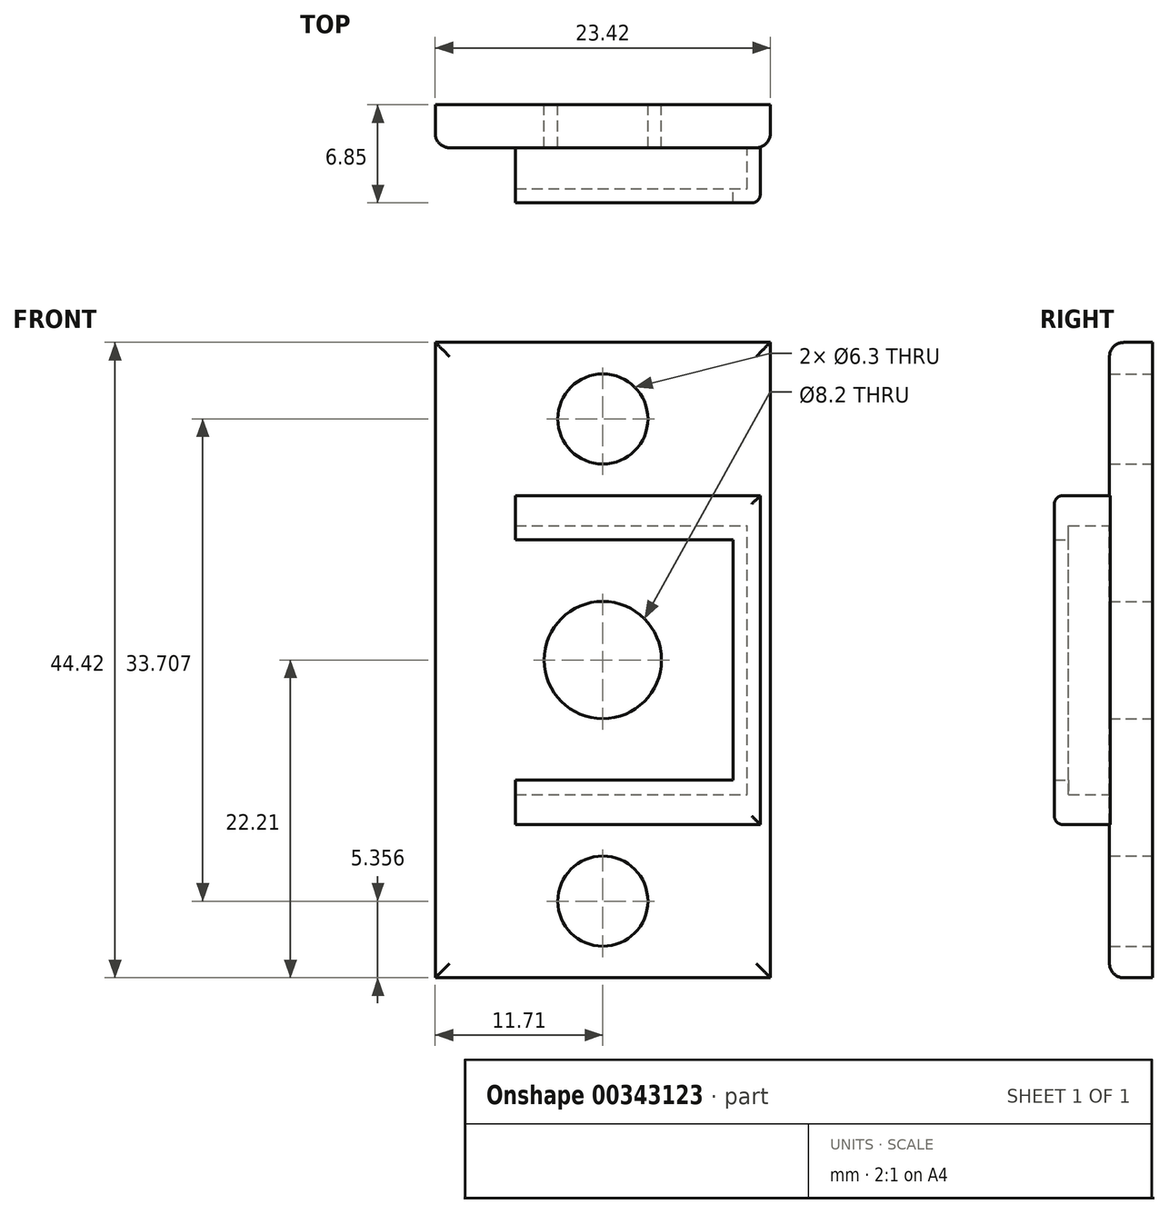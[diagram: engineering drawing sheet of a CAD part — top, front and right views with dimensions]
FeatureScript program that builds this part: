
annotation { "Feature Type Name" : "Feature", "Feature Type Description" : "" }
export const myFeature = defineFeature(function(context is Context, id is Id, definition is map)
    precondition{}
    {
        {
            var Q0;
            Q0=qCreatedBy(makeId("Front.planeOp"),FACE);
            var sketch = newSketch(context, id + "F0", { "sketchPlane" : qUnion([Q0])});
            skLineSegment(sketch, "E0.bottom", {"start": v(0, 0) * mm, "end": v(22, 0) * mm});
            skLineSegment(sketch, "E0.top", {"start": v(0, 23) * mm, "end": v(22, 23) * mm});
            skLineSegment(sketch, "E0.left", {"start": v(0, 0) * mm, "end": v(0, 23) * mm});
            skLineSegment(sketch, "E0.right", {"start": v(22, 0) * mm, "end": v(22, 23) * mm});
            skLineSegment(sketch, "E1.bottom", {"start": v(21.1, 20.9) * mm, "end": v(0.9, 20.9) * mm});
            skLineSegment(sketch, "E1.top", {"start": v(21.1, 2.1) * mm, "end": v(0.9, 2.1) * mm});
            skLineSegment(sketch, "E1.left", {"start": v(21.1, 20.9) * mm, "end": v(21.1, 2.1) * mm});
            skLineSegment(sketch, "E1.right", {"start": v(0.9, 20.9) * mm, "end": v(0.9, 2.1) * mm});
            skPoint(sketch, "E2", {"position": v(4.9, 20.9) * mm});
            skPoint(sketch, "E3", {"position": v(4.9, 2.1) * mm});
            skPoint(sketch, "E4", {"position": v(22, 1.5) * mm});
            skPoint(sketch, "E5", {"position": v(22, 21.5) * mm});
            skPoint(sketch, "E6", {"position": v(0, 1.5) * mm});
            skPoint(sketch, "E7", {"position": v(11, 11.5) * mm});
            skLineSegment(sketch, "E8", {"start": v(4.9, 20.9) * mm, "end": v(4.9, 23) * mm});
            skLineSegment(sketch, "E9", {"start": v(4.9, 2.1) * mm, "end": v(4.9, 0) * mm});
            skPoint(sketch, "E10", {"position": v(11, 20.9) * mm});
            skPoint(sketch, "E11", {"position": v(11, 2.1) * mm});
            skLineSegment(sketch, "E12.bottom", {"start": v(22.7, 33.7) * mm, "end": v(-0.7, 33.7) * mm});
            skLineSegment(sketch, "E12.top", {"start": v(22.7, -10.7) * mm, "end": v(-0.7, -10.7) * mm});
            skLineSegment(sketch, "E12.left", {"start": v(22.7, 33.7) * mm, "end": v(22.7, -10.7) * mm});
            skLineSegment(sketch, "E12.right", {"start": v(-0.7, 33.7) * mm, "end": v(-0.7, -10.7) * mm});
            skPoint(sketch, "E13", {"position": v(11, -5.35) * mm});
            skPoint(sketch, "E14", {"position": v(11, 28.35) * mm});
            skLineSegment(sketch, "E15", {"start": v(11, 29.06) * mm, "end": v(11, 27.39) * mm});
            skLineSegment(sketch, "E16", {"start": v(11, -4.63) * mm, "end": v(11, -5.92) * mm});
            skSolve(sketch);
        }
        {
            var Q0;
            Q0=makeQuery(id+"F0.imprint","IMPRINT",FACE,{"disambiguationData":[TD([[makeQuery(id+"F0.imprint","IMPRINT",EDGE,{"derivedFrom":sQuery(id+"F0.wireOp",EDGE,"E1.bottom")}),1.0]])]});
            var Q1;
            Q1=makeQuery(id+"F0.imprint","IMPRINT",FACE,{"disambiguationData":[TD([[makeQuery(id+"F0.imprint","IMPRINT",EDGE,{"derivedFrom":sQuery(id+"F0.wireOp",EDGE,"E0.bottom")}),1.0]])]});
            extrude(context, id + "F1", {"entities" : qUnion([Q0, Q1]), "depth" : 3 * mm});
        }
        {
            var Q0;
            {var subQ0=sQuery(id+"F0.wireOp",EDGE,"E0.right");Q0=makeQuery(id+"F0.imprint","IMPRINT",FACE,{"disambiguationData":[TD([[makeQuery(id+"F0.imprint","IMPRINT",EDGE,{"derivedFrom":subQ0}),1.0]])]});}
            extrude(context, id + "F2", {"entities" : qUnion([Q0]), "operationType" : NewBodyOperationType.ADD, "depth" : 6.85 * mm});
        }
        {
            var Q0;
            Q0=makeQuery(id+"F2.opExtrude","SWEPT_FACE",FACE,{"disambiguationData":[OSD([sQuery(id+"F0.wireOp",EDGE,"E1.bottom")])]});
            var sketch = newSketch(context, id + "F3", { "sketchPlane" : qUnion([Q0])});
            skLineSegment(sketch, "E17.bottom", {"start": v(21.1, 6.85) * mm, "end": v(21.1, 6.85) * mm});
            skLineSegment(sketch, "E17.top", {"start": v(21.1, 5.85) * mm, "end": v(21.1, 5.85) * mm});
            skLineSegment(sketch, "E17.left", {"start": v(21.1, 6.85) * mm, "end": v(21.1, 5.85) * mm});
            skLineSegment(sketch, "E17.right", {"start": v(21.1, 6.85) * mm, "end": v(21.1, 5.85) * mm});
            skLineSegment(sketch, "E18.bottom", {"start": v(4.9, 6.85) * mm, "end": v(21.1, 6.85) * mm});
            skLineSegment(sketch, "E18.top", {"start": v(4.9, 5.85) * mm, "end": v(21.1, 5.85) * mm});
            skLineSegment(sketch, "E18.left", {"start": v(4.9, 6.85) * mm, "end": v(4.9, 5.85) * mm});
            skSolve(sketch);
        }
        {
            var Q0;
            Q0=makeQuery(id+"F2.opExtrude","SWEPT_FACE",FACE,{"disambiguationData":[OSD([sQuery(id+"F0.wireOp",EDGE,"E1.left")])]});
            var sketch = newSketch(context, id + "F4", { "sketchPlane" : qUnion([Q0])});
            skLineSegment(sketch, "E19.bottom", {"start": v(6.85, 2.1) * mm, "end": v(5.85, 2.1) * mm});
            skLineSegment(sketch, "E19.top", {"start": v(6.85, 20.9) * mm, "end": v(5.85, 20.9) * mm});
            skLineSegment(sketch, "E19.left", {"start": v(6.85, 2.1) * mm, "end": v(6.85, 20.9) * mm});
            skLineSegment(sketch, "E19.right", {"start": v(5.85, 2.1) * mm, "end": v(5.85, 20.9) * mm});
            skSolve(sketch);
        }
        {
            var Q0;
            Q0=makeQuery(id+"F2.opExtrude","SWEPT_FACE",FACE,{"disambiguationData":[OSD([sQuery(id+"F0.wireOp",EDGE,"E1.top")])]});
            var sketch = newSketch(context, id + "F5", { "sketchPlane" : qUnion([Q0])});
            skLineSegment(sketch, "E20.bottom", {"start": v(21.1, -6.85) * mm, "end": v(21.1, -6.85) * mm});
            skLineSegment(sketch, "E20.top", {"start": v(21.1, -5.85) * mm, "end": v(21.1, -5.85) * mm});
            skLineSegment(sketch, "E20.left", {"start": v(21.1, -6.85) * mm, "end": v(21.1, -5.85) * mm});
            skLineSegment(sketch, "E20.right", {"start": v(21.1, -6.85) * mm, "end": v(21.1, -5.85) * mm});
            skLineSegment(sketch, "E21.bottom", {"start": v(4.9, -6.85) * mm, "end": v(21.1, -6.85) * mm});
            skLineSegment(sketch, "E21.top", {"start": v(4.9, -5.85) * mm, "end": v(21.1, -5.85) * mm});
            skLineSegment(sketch, "E21.left", {"start": v(4.9, -6.85) * mm, "end": v(4.9, -5.85) * mm});
            skSolve(sketch);
        }
        {
            var Q0;
            {var subQ4=sQuery(id+"F0.wireOp",EDGE,"E0.left");Q0=makeQuery(id+"F0.imprint","IMPRINT",FACE,{"disambiguationData":[TD([[makeQuery(id+"F0.imprint","IMPRINT",EDGE,{"derivedFrom":subQ4}),-1.0]])]});}
            extrude(context, id + "F6", {"entities" : qUnion([Q0]), "operationType" : NewBodyOperationType.ADD, "depth" : 3 * mm});
        }
        {
            var Q0;
            Q0=makeQuery(id+"F3.imprint","IMPRINT",FACE,{"disambiguationData":[TD([[makeQuery(id+"F3.imprint","IMPRINT",EDGE,{"derivedFrom":sQuery(id+"F3.wireOp",EDGE,"E17.bottom")}),1.0]])]});
            var Q1;
            Q1=makeQuery(id+"F3.imprint","IMPRINT",FACE,{"disambiguationData":[TD([[makeQuery(id+"F3.imprint","IMPRINT",EDGE,{"derivedFrom":sQuery(id+"F3.wireOp",EDGE,"E18.bottom")}),1.0]])]});
            extrude(context, id + "F7", {"entities" : qUnion([Q0, Q1]), "operationType" : NewBodyOperationType.ADD, "depth" : 1 * mm});
        }
        {
            var Q0;
            Q0=makeQuery(id+"F5.imprint","IMPRINT",FACE,{"disambiguationData":[TD([[makeQuery(id+"F5.imprint","IMPRINT",EDGE,{"derivedFrom":sQuery(id+"F5.wireOp",EDGE,"E20.bottom")}),-1.0]])]});
            var Q1;
            Q1=makeQuery(id+"F5.imprint","IMPRINT",FACE,{"disambiguationData":[TD([[makeQuery(id+"F5.imprint","IMPRINT",EDGE,{"derivedFrom":sQuery(id+"F5.wireOp",EDGE,"E21.bottom")}),-1.0]])]});
            extrude(context, id + "F8", {"entities" : qUnion([Q0, Q1]), "operationType" : NewBodyOperationType.ADD, "depth" : 1 * mm});
        }
        {
            var Q0;
            Q0=makeQuery(id+"F4.imprint","IMPRINT",FACE,{"disambiguationData":[TD([[makeQuery(id+"F4.imprint","IMPRINT",EDGE,{"derivedFrom":sQuery(id+"F4.wireOp",EDGE,"E19.bottom")}),-1.0]])]});
            extrude(context, id + "F9", {"entities" : qUnion([Q0]), "operationType" : NewBodyOperationType.ADD, "depth" : 1 * mm});
        }
        {
            var Q0;
            Q0=sQuery(id+"F0.wireOp",VERTEX,"E7");
            var Q1;
            Q1=makeQuery(id+"F1.opExtrude","SWEPT_BODY",BODY,{"disambiguationData":[OSD([sQuery(id+"F0.wireOp",EDGE,"E0.bottom"),sQuery(id+"F0.wireOp",EDGE,"E0.top"),sQuery(id+"F0.wireOp",EDGE,"E0.right"),sQuery(id+"F0.wireOp",EDGE,"E1.bottom"),sQuery(id+"F0.wireOp",EDGE,"E1.top"),sQuery(id+"F0.wireOp",EDGE,"E1.right"),sQuery(id+"F0.wireOp",EDGE,"IjJQbh8V-s165-LqST-yhQQ-smVxdiDUJUNB"),sQuery(id+"F0.wireOp",EDGE,"vMIWCNPO-odwN-dmoI-aRjE-b61Hn6vikTsy"),sQuery(id+"F0.wireOp",EDGE,"QBn7oY1Y-4jN5-nkhJ-HE16-C3luuC495pl6.bottom"),sQuery(id+"F0.wireOp",EDGE,"CAiNjQEx-sT3u-gWMX-P0WK-hNQpG0efZflQ.bottom"),sQuery(id+"F0.wireOp",EDGE,"AEsHusZ2-MIhm-eAMg-T6Nq-u61gnZOwzoZV.bottom"),sQuery(id+"F0.wireOp",EDGE,"Er4cVGr4-94Hq-jv4w-pvqk-ljwNyZ9HIM5P.bottom")])]});
            hole(context, id + "F10", {"style" : HoleStyle.SIMPLE, "endStyle" : HoleEndStyle.THROUGH, "oppositeDirection" : true, "holeDiameter" : 8.2 * mm, "tappedDepth" : 12 * mm, "tapClearance" : 3, "locations" : qUnion([Q0]), "scope" : qUnion([Q1])});
        }
        {
            var Q0;
            {var subQ3=sQuery(id+"F0.wireOp",EDGE,"E0.left");Q0=makeQuery(id+"F0.imprint","IMPRINT",FACE,{"disambiguationData":[TD([[makeQuery(id+"F0.imprint","IMPRINT",EDGE,{"derivedFrom":subQ3}),1.0]])]});}
            extrude(context, id + "F11", {"entities" : qUnion([Q0]), "operationType" : NewBodyOperationType.ADD, "depth" : 3 * mm});
        }
        {
            var Q0;
            Q0=makeQuery(id+"F11.opExtrude","CAP_EDGE",EDGE,{"disambiguationData":[OSD([sQuery(id+"F0.wireOp",EDGE,"E12.top")])],"isStart":false});
            var Q1;
            Q1=makeQuery(id+"F11.opExtrude","CAP_EDGE",EDGE,{"disambiguationData":[OSD([sQuery(id+"F0.wireOp",EDGE,"E12.right")])],"isStart":false});
            var Q2;
            Q2=makeQuery(id+"F11.opExtrude","CAP_EDGE",EDGE,{"disambiguationData":[OSD([sQuery(id+"F0.wireOp",EDGE,"E12.bottom")])],"isStart":false});
            var Q3;
            Q3=makeQuery(id+"F11.opExtrude","CAP_EDGE",EDGE,{"disambiguationData":[OSD([sQuery(id+"F0.wireOp",EDGE,"E12.left")])],"isStart":false});
            fillet(context, id + "F12", {"entities" : qUnion([Q0, Q1, Q2, Q3]), "radius" : 1 * mm, "tangentPropagation" : true, "allowEdgeOverflow" : false});
        }
        {
            var Q0;
            Q0=makeQuery(id+"F2.opExtrude","CAP_EDGE",EDGE,{"disambiguationData":[OSD([sQuery(id+"F0.wireOp",EDGE,"E0.right")])],"isStart":false});
            var Q1;
            Q1=makeQuery(id+"F2.opExtrude","CAP_EDGE",EDGE,{"disambiguationData":[OSD([sQuery(id+"F0.wireOp",EDGE,"E0.bottom")])],"isStart":false});
            var Q2;
            Q2=makeQuery(id+"F2.opExtrude","CAP_EDGE",EDGE,{"disambiguationData":[OSD([sQuery(id+"F0.wireOp",EDGE,"E0.top")])],"isStart":false});
            fillet(context, id + "F13", {"entities" : qUnion([Q0, Q1, Q2]), "radius" : 0.6 * mm, "tangentPropagation" : true, "allowEdgeOverflow" : false});
        }
        {
            var Q0;
            Q0=sQuery(id+"F0.wireOp",VERTEX,"E14");
            var Q1;
            Q1=sQuery(id+"F0.wireOp",VERTEX,"E13");
            var Q2;
            Q2=makeQuery(id+"F1.opExtrude","SWEPT_BODY",BODY,{"disambiguationData":[OSD([sQuery(id+"F0.wireOp",EDGE,"E0.bottom"),sQuery(id+"F0.wireOp",EDGE,"E0.top"),sQuery(id+"F0.wireOp",EDGE,"E0.left"),sQuery(id+"F0.wireOp",EDGE,"E0.right")])]});
            hole(context, id + "F14", {"style" : HoleStyle.SIMPLE, "endStyle" : HoleEndStyle.THROUGH, "oppositeDirection" : true, "holeDiameter" : 6.3 * mm, "isTappedThrough" : true, "tappedDepth" : 12 * mm, "tapClearance" : 3, "locations" : qUnion([Q0, Q1]), "scope" : qUnion([Q2])});
        }
    });
